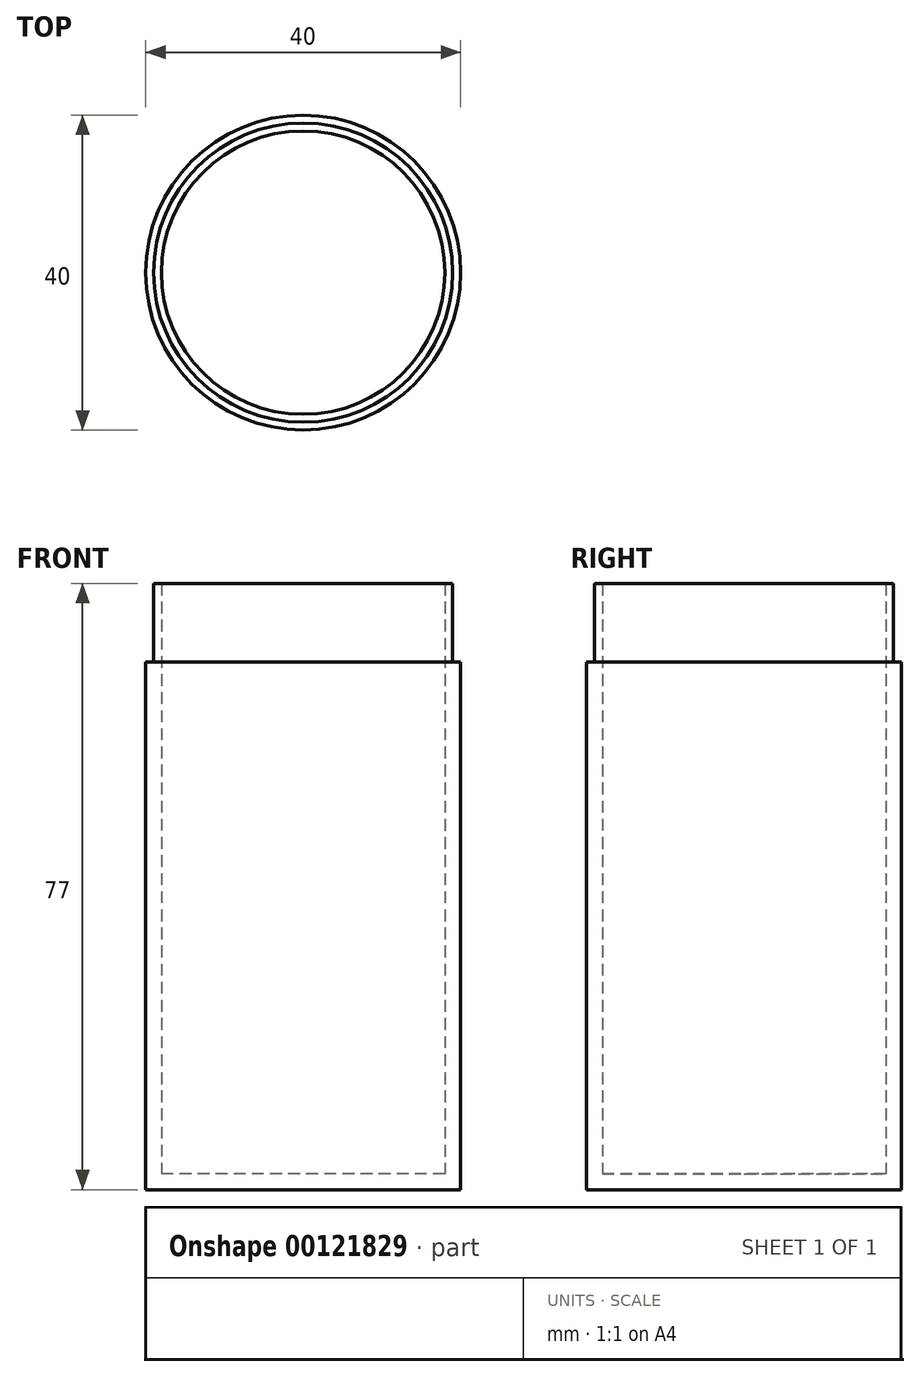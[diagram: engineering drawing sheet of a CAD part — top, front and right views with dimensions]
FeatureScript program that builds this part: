
annotation { "Feature Type Name" : "Feature", "Feature Type Description" : "" }
export const myFeature = defineFeature(function(context is Context, id is Id, definition is map)
    precondition{}
    {
        {
            var Q0;
            Q0=qCreatedBy(makeId("Top.planeOp"),FACE);
            var sketch = newSketch(context, id + "F0", { "sketchPlane" : qUnion([Q0])});
            skCircle(sketch, "E0", {"center": v(0, 0) * mm, "radius": 20 * mm});
            skSolve(sketch);
        }
        {
            var Q0;
            Q0=makeQuery(id+"F0.imprint","IMPRINT",FACE,{"disambiguationData":[TD([[makeQuery(id+"F0.imprint","IMPRINT",EDGE,{"derivedFrom":sQuery(id+"F0.wireOp",EDGE,"E0")}),1.0]])]});
            extrude(context, id + "F1", {"entities" : qUnion([Q0]), "depth" : 2 * mm});
        }
        {
            var Q0;
            Q0=makeQuery(id+"F1.opExtrude","CAP_FACE",FACE,{"disambiguationData":[OSD([sQuery(id+"F0.wireOp",EDGE,"E0")])],"isStart":false});
            var sketch = newSketch(context, id + "F2", { "sketchPlane" : qUnion([Q0])});
            skCircle(sketch, "E1", {"center": v(0, 0) * mm, "radius": 18 * mm});
            skSolve(sketch);
        }
        {
            var Q0;
            Q0=makeQuery(id+"F2.imprint","IMPRINT",FACE,{"disambiguationData":[TD([[makeQuery(id+"F2.imprint","IMPRINT",EDGE,{"derivedFrom":sQuery(id+"F2.wireOp",EDGE,"E1")}),-1.0]])]});
            extrude(context, id + "F3", {"entities" : qUnion([Q0]), "operationType" : NewBodyOperationType.ADD, "depth" : 75 * mm});
        }
        {
            var Q0;
            Q0=makeQuery(id+"F3.opExtrude","CAP_FACE",FACE,{"disambiguationData":[OSD([sQuery(id+"F0.wireOp",EDGE,"E0"),sQuery(id+"F2.wireOp",EDGE,"E1")])],"isStart":false});
            var sketch = newSketch(context, id + "F4", { "sketchPlane" : qUnion([Q0])});
            skCircle(sketch, "E2", {"center": v(0, 0) * mm, "radius": 19 * mm});
            skSolve(sketch);
        }
        {
            var Q0;
            Q0=makeQuery(id+"F4.imprint","IMPRINT",FACE,{"disambiguationData":[TD([[makeQuery(id+"F4.imprint","IMPRINT",EDGE,{"derivedFrom":sQuery(id+"F4.wireOp",EDGE,"E2")}),-1.0]])]});
            extrude(context, id + "F5", {"entities" : qUnion([Q0]), "operationType" : NewBodyOperationType.REMOVE, "oppositeDirection" : true, "depth" : 10 * mm});
        }
    });
